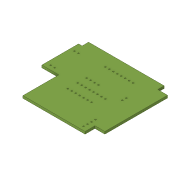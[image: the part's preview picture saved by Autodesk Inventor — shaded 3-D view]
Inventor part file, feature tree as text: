
AUTODESK INVENTOR PART (.ipt)
format: ipt  version: 2017 (Build 210142000, 142)  size: 172,032 bytes
history: native  units: in
note: dims shown in document units (in); Inventor stores cm internally (conversion verified against a paired STEP export)
features: extrude x1, sketch x1
ambient origin geometry x8: Origin, YZ Plane, XZ Plane, XY Plane, X Axis, Y Axis, Z Axis, Center Point
bodies: Solid1 (feature_tree)
feature tree (2):
  extrude  "Extrusion1"  Depth=2.0in
  sketch  "Sketch1"  dims[d0=2.25in d1=2.0in d2=0.164in d3=0.25in d4=0.25in d5=0.43in d6=0.908in d7=0.09in d8=0.035in d9=0.1in d10=0.109in d11=0.375in d12=0.035in d13=0.1in d14=0.106in d15=0.118in d16=0.1in d17=0.1in d18=0.1in d19=0.1in d20=0.1in d21=0.1in d22=0.1in d23=0.331in d24=0.846in d25=0.1in d26=0.1in d27=0.1in d28=0.1in d29=0.1in d30=0.1in d31=0.1in d32=0.7in d33=0.1in d34=0.1in d35=0.1in d36=0.1in d37=0.1in d38=0.1in d39=0.25in d40=0.1in d41=0.1in d42=0.1in d44=0.1in d45=0.1in d46=0.1in d47=0.091in d48=0.128in d49=0.007in d50=0.219in d51=0.1in d52=0.586in d53=0.458in d54=0.06in d55=0.0in]
